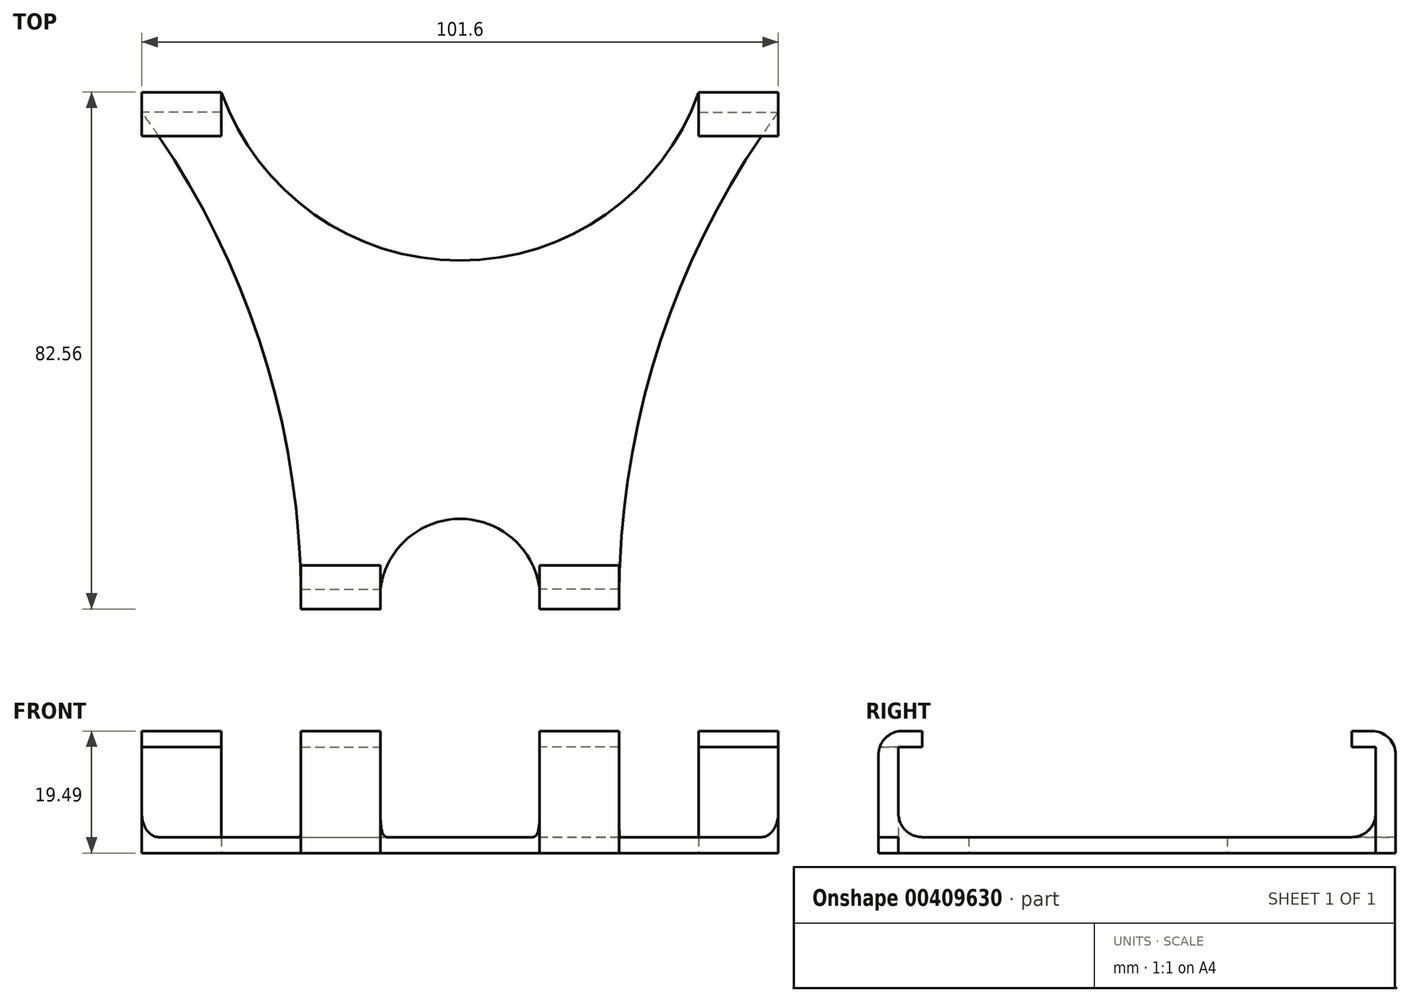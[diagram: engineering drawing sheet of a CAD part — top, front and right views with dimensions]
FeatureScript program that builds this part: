
annotation { "Feature Type Name" : "Feature", "Feature Type Description" : "" }
export const myFeature = defineFeature(function(context is Context, id is Id, definition is map)
    precondition{}
    {
        {
            var Q0;
            Q0=qCreatedBy(makeId("Top.planeOp"),FACE);
            var sketch = newSketch(context, id + "F0", { "sketchPlane" : qUnion([Q0])});
            skPoint(sketch, "E0.middle", {"position": v(0, 0) * mm});
            skLineSegment(sketch, "E1.bottom", {"start": v(-38.1, 38.1) * mm, "end": v(-50.8, 38.1) * mm});
            skLineSegment(sketch, "E1.top", {"start": v(-38.1, 41.27) * mm, "end": v(-50.8, 41.27) * mm});
            skLineSegment(sketch, "E1.left", {"start": v(-38.1, 38.1) * mm, "end": v(-38.1, 41.27) * mm});
            skLineSegment(sketch, "E1.right", {"start": v(-50.8, 38.1) * mm, "end": v(-50.8, 41.27) * mm});
            skLineSegment(sketch, "E2.bottom", {"start": v(-25.4, -38.1) * mm, "end": v(-12.7, -38.1) * mm});
            skLineSegment(sketch, "E2.top", {"start": v(-25.4, -41.28) * mm, "end": v(-12.7, -41.28) * mm});
            skLineSegment(sketch, "E2.left", {"start": v(-25.4, -38.1) * mm, "end": v(-25.4, -41.28) * mm});
            skLineSegment(sketch, "E2.right", {"start": v(-12.7, -38.1) * mm, "end": v(-12.7, -41.28) * mm});
            skLineSegment(sketch, "E3.MirrorCS", {"start": v(50.8, 38.1) * mm, "end": v(50.8, 41.27) * mm});
            skLineSegment(sketch, "E4.MirrorCS", {"start": v(38.1, 38.1) * mm, "end": v(38.1, 41.27) * mm});
            skLineSegment(sketch, "E5.MirrorCS", {"start": v(38.1, 41.27) * mm, "end": v(50.8, 41.27) * mm});
            skLineSegment(sketch, "E6.MirrorCS", {"start": v(38.1, 38.1) * mm, "end": v(50.8, 38.1) * mm});
            skLineSegment(sketch, "E7.MirrorCS", {"start": v(12.7, -38.1) * mm, "end": v(12.7, -41.28) * mm});
            skLineSegment(sketch, "E8.MirrorCS", {"start": v(25.4, -38.1) * mm, "end": v(25.4, -41.28) * mm});
            skLineSegment(sketch, "E9.MirrorCS", {"start": v(25.4, -38.1) * mm, "end": v(12.7, -38.1) * mm});
            skLineSegment(sketch, "E10.MirrorCS", {"start": v(25.4, -41.28) * mm, "end": v(12.7, -41.28) * mm});
            skArc(sketch, "E11", {"start": v(-25.4, -41.28) * mm, "mid": v(-31.66, 0.47) * mm, "end": v(-50.8, 38.1) * mm});
            skArc(sketch, "E12", {"start": v(50.8, 38.1) * mm, "mid": v(31.66, 0.47) * mm, "end": v(25.4, -41.27) * mm});
            skArc(sketch, "E13", {"start": v(-38.1, 41.27) * mm, "mid": v(0, 14.38) * mm, "end": v(38.1, 41.27) * mm});
            skArc(sketch, "E14", {"start": v(12.7, -41.28) * mm, "mid": v(0, -26.89) * mm, "end": v(-12.7, -41.27) * mm});
            skSolve(sketch);
        }
        {
            var Q0;
            Q0=makeQuery(id+"F0.imprint","IMPRINT",FACE,{"disambiguationData":[TD([[makeQuery(id+"F0.imprint","IMPRINT",EDGE,{"derivedFrom":sQuery(id+"F0.wireOp",EDGE,"E1.bottom")}),-1.0]])]});
            var Q1;
            Q1=makeQuery(id+"F0.imprint","IMPRINT",FACE,{"disambiguationData":[TD([[makeQuery(id+"F0.imprint","IMPRINT",EDGE,{"derivedFrom":sQuery(id+"F0.wireOp",EDGE,"E2.bottom")}),-1.0]])]});
            var Q2;
            Q2=makeQuery(id+"F0.imprint","IMPRINT",FACE,{"disambiguationData":[TD([[makeQuery(id+"F0.imprint","IMPRINT",EDGE,{"derivedFrom":sQuery(id+"F0.wireOp",EDGE,"E3.MirrorCS")}),1.0]])]});
            var Q3;
            Q3=makeQuery(id+"F0.imprint","IMPRINT",FACE,{"disambiguationData":[TD([[makeQuery(id+"F0.imprint","IMPRINT",EDGE,{"derivedFrom":sQuery(id+"F0.wireOp",EDGE,"E7.MirrorCS")}),1.0]])]});
            var Q4;
            {var subQ0=sQuery(id+"F0.wireOp",EDGE,"E9.MirrorCS");Q4=makeQuery(id+"F0.imprint","IMPRINT",FACE,{"disambiguationData":[TD([[makeQuery(id+"F0.imprint","IMPRINT",EDGE,{"derivedFrom":subQ0}),1.0]])]});}
            extrude(context, id + "F1", {"entities" : qUnion([Q0, Q1, Q2, Q3, Q4]), "depth" : 16.95 * mm});
        }
        {
            var Q0;
            Q0 = qSketchRegion(id + "F0", true);
            extrude(context, id + "F2", {"entities" : qUnion([Q0]), "operationType" : NewBodyOperationType.ADD, "depth" : 2.54 * mm});
        }
        {
            var Q0;
            Q0=makeQuery(id+"F1.opExtrude","CAP_FACE",FACE,{"disambiguationData":[OSD([sQuery(id+"F0.wireOp",EDGE,"E1.bottom"),sQuery(id+"F0.wireOp",EDGE,"E1.top"),sQuery(id+"F0.wireOp",EDGE,"E1.left"),sQuery(id+"F0.wireOp",EDGE,"E1.right")])],"isStart":false});
            var sketch = newSketch(context, id + "F3", { "sketchPlane" : qUnion([Q0])});
            skLineSegment(sketch, "E15.bottom", {"start": v(-50.8, 41.27) * mm, "end": v(-38.1, 41.27) * mm});
            skLineSegment(sketch, "E15.top", {"start": v(-50.8, 34.29) * mm, "end": v(-38.1, 34.29) * mm});
            skLineSegment(sketch, "E15.left", {"start": v(-50.8, 41.27) * mm, "end": v(-50.8, 34.29) * mm});
            skLineSegment(sketch, "E15.right", {"start": v(-38.1, 41.27) * mm, "end": v(-38.1, 34.29) * mm});
            skLineSegment(sketch, "E16.MirrorCS", {"start": v(50.8, 41.27) * mm, "end": v(38.1, 41.27) * mm});
            skLineSegment(sketch, "E17.MirrorCS", {"start": v(50.8, 41.27) * mm, "end": v(50.8, 34.29) * mm});
            skLineSegment(sketch, "E18.MirrorCS", {"start": v(50.8, 34.29) * mm, "end": v(38.1, 34.29) * mm});
            skLineSegment(sketch, "E19.MirrorCS", {"start": v(38.1, 41.27) * mm, "end": v(38.1, 34.29) * mm});
            skSolve(sketch);
        }
        {
            var Q0;
            Q0 = qSketchRegion(id + "F3", true);
            extrude(context, id + "F4", {"entities" : qUnion([Q0]), "operationType" : NewBodyOperationType.ADD, "depth" : 2.54 * mm});
        }
        {
            var Q0;
            Q0=makeQuery(id+"F1.opExtrude","CAP_FACE",FACE,{"disambiguationData":[OSD([sQuery(id+"F0.wireOp",EDGE,"E2.bottom"),sQuery(id+"F0.wireOp",EDGE,"E2.top"),sQuery(id+"F0.wireOp",EDGE,"E2.left"),sQuery(id+"F0.wireOp",EDGE,"E2.right")])],"isStart":false});
            var sketch = newSketch(context, id + "F5", { "sketchPlane" : qUnion([Q0])});
            skLineSegment(sketch, "E20.bottom", {"start": v(-25.4, -41.28) * mm, "end": v(-12.7, -41.28) * mm});
            skLineSegment(sketch, "E20.top", {"start": v(-25.4, -34.3) * mm, "end": v(-12.7, -34.3) * mm});
            skLineSegment(sketch, "E20.left", {"start": v(-25.4, -41.28) * mm, "end": v(-25.4, -34.3) * mm});
            skLineSegment(sketch, "E20.right", {"start": v(-12.7, -41.28) * mm, "end": v(-12.7, -34.3) * mm});
            skLineSegment(sketch, "E21.MirrorCS", {"start": v(12.7, -41.28) * mm, "end": v(12.7, -34.3) * mm});
            skLineSegment(sketch, "E22.MirrorCS", {"start": v(25.4, -41.28) * mm, "end": v(25.4, -34.3) * mm});
            skLineSegment(sketch, "E23.MirrorCS", {"start": v(25.4, -41.28) * mm, "end": v(12.7, -41.28) * mm});
            skLineSegment(sketch, "E24.MirrorCS", {"start": v(25.4, -34.3) * mm, "end": v(12.7, -34.3) * mm});
            skSolve(sketch);
        }
        {
            var Q0;
            Q0 = qSketchRegion(id + "F5", true);
            extrude(context, id + "F6", {"entities" : qUnion([Q0]), "operationType" : NewBodyOperationType.ADD, "depth" : 2.54 * mm});
        }
        {
            var Q0;
            Q0=makeQuery(id+"F2.boolean.opBoolean","INTERSECT",EDGE,{"derivedFrom":[makeQuery(id+"F1.opExtrude","SWEPT_FACE",FACE,{"disambiguationData":[OSD([sQuery(id+"F0.wireOp",EDGE,"E1.bottom")])]}),makeQuery(id+"F2.opExtrude","CAP_FACE",FACE,{"disambiguationData":[OSD([sQuery(id+"F0.wireOp",EDGE,"E1.top"),sQuery(id+"F0.wireOp",EDGE,"E1.right"),sQuery(id+"F0.wireOp",EDGE,"E2.top"),sQuery(id+"F0.wireOp",EDGE,"E3.MirrorCS"),sQuery(id+"F0.wireOp",EDGE,"E5.MirrorCS"),sQuery(id+"F0.wireOp",EDGE,"E10.MirrorCS"),sQuery(id+"F0.wireOp",EDGE,"hXJoZnsT-Lg7h-pbVR-MQxj-FSggZeGGHfwX"),sQuery(id+"F0.wireOp",EDGE,"yavpTBRq-CuO9-Qr0M-t35S-z9Fk4aJHSNEh"),sQuery(id+"F0.wireOp",EDGE,"0S22i0gG-gJf3-JBYY-297k-QcKDuxpLSIet"),sQuery(id+"F0.wireOp",EDGE,"gkpGqHkD-Pt0P-Dbue-5Zzd-4DBEraHI7jx1")])],"isStart":false})]});
            var Q1;
            Q1=makeQuery(id+"F1.opExtrude","CAP_EDGE",EDGE,{"disambiguationData":[OSD([sQuery(id+"F0.wireOp",EDGE,"E1.bottom")])],"isStart":false});
            var Q2;
            Q2=makeQuery(id+"F2.boolean.opBoolean","INTERSECT",EDGE,{"derivedFrom":[makeQuery(id+"F1.opExtrude","SWEPT_FACE",FACE,{"disambiguationData":[OSD([sQuery(id+"F0.wireOp",EDGE,"E6.MirrorCS")])]}),makeQuery(id+"F2.opExtrude","CAP_FACE",FACE,{"disambiguationData":[OSD([sQuery(id+"F0.wireOp",EDGE,"E1.top"),sQuery(id+"F0.wireOp",EDGE,"E1.right"),sQuery(id+"F0.wireOp",EDGE,"E2.top"),sQuery(id+"F0.wireOp",EDGE,"E3.MirrorCS"),sQuery(id+"F0.wireOp",EDGE,"E5.MirrorCS"),sQuery(id+"F0.wireOp",EDGE,"E10.MirrorCS"),sQuery(id+"F0.wireOp",EDGE,"hXJoZnsT-Lg7h-pbVR-MQxj-FSggZeGGHfwX"),sQuery(id+"F0.wireOp",EDGE,"yavpTBRq-CuO9-Qr0M-t35S-z9Fk4aJHSNEh"),sQuery(id+"F0.wireOp",EDGE,"0S22i0gG-gJf3-JBYY-297k-QcKDuxpLSIet"),sQuery(id+"F0.wireOp",EDGE,"gkpGqHkD-Pt0P-Dbue-5Zzd-4DBEraHI7jx1")])],"isStart":false})]});
            var Q3;
            Q3=makeQuery(id+"F1.opExtrude","CAP_EDGE",EDGE,{"disambiguationData":[OSD([sQuery(id+"F0.wireOp",EDGE,"E6.MirrorCS")])],"isStart":false});
            var Q4;
            Q4=makeQuery(id+"F2.boolean.opBoolean","INTERSECT",EDGE,{"derivedFrom":[makeQuery(id+"F1.opExtrude","SWEPT_FACE",FACE,{"disambiguationData":[OSD([sQuery(id+"F0.wireOp",EDGE,"E2.bottom")])]}),makeQuery(id+"F2.opExtrude","CAP_FACE",FACE,{"disambiguationData":[OSD([sQuery(id+"F0.wireOp",EDGE,"E1.top"),sQuery(id+"F0.wireOp",EDGE,"E1.right"),sQuery(id+"F0.wireOp",EDGE,"E2.top"),sQuery(id+"F0.wireOp",EDGE,"E3.MirrorCS"),sQuery(id+"F0.wireOp",EDGE,"E5.MirrorCS"),sQuery(id+"F0.wireOp",EDGE,"E10.MirrorCS"),sQuery(id+"F0.wireOp",EDGE,"hXJoZnsT-Lg7h-pbVR-MQxj-FSggZeGGHfwX"),sQuery(id+"F0.wireOp",EDGE,"yavpTBRq-CuO9-Qr0M-t35S-z9Fk4aJHSNEh"),sQuery(id+"F0.wireOp",EDGE,"0S22i0gG-gJf3-JBYY-297k-QcKDuxpLSIet"),sQuery(id+"F0.wireOp",EDGE,"gkpGqHkD-Pt0P-Dbue-5Zzd-4DBEraHI7jx1")])],"isStart":false})]});
            var Q5;
            Q5=makeQuery(id+"F2.boolean.opBoolean","INTERSECT",EDGE,{"derivedFrom":[makeQuery(id+"F1.opExtrude","SWEPT_FACE",FACE,{"disambiguationData":[OSD([sQuery(id+"F0.wireOp",EDGE,"E9.MirrorCS")])]}),makeQuery(id+"F2.opExtrude","CAP_FACE",FACE,{"disambiguationData":[OSD([sQuery(id+"F0.wireOp",EDGE,"E1.top"),sQuery(id+"F0.wireOp",EDGE,"E1.right"),sQuery(id+"F0.wireOp",EDGE,"E2.top"),sQuery(id+"F0.wireOp",EDGE,"E3.MirrorCS"),sQuery(id+"F0.wireOp",EDGE,"E5.MirrorCS"),sQuery(id+"F0.wireOp",EDGE,"E10.MirrorCS"),sQuery(id+"F0.wireOp",EDGE,"hXJoZnsT-Lg7h-pbVR-MQxj-FSggZeGGHfwX"),sQuery(id+"F0.wireOp",EDGE,"yavpTBRq-CuO9-Qr0M-t35S-z9Fk4aJHSNEh"),sQuery(id+"F0.wireOp",EDGE,"0S22i0gG-gJf3-JBYY-297k-QcKDuxpLSIet"),sQuery(id+"F0.wireOp",EDGE,"gkpGqHkD-Pt0P-Dbue-5Zzd-4DBEraHI7jx1")])],"isStart":false})]});
            var Q6;
            Q6=makeQuery(id+"F1.opExtrude","CAP_EDGE",EDGE,{"disambiguationData":[OSD([sQuery(id+"F0.wireOp",EDGE,"E9.MirrorCS")])],"isStart":false});
            var Q7;
            Q7=makeQuery(id+"F1.opExtrude","CAP_EDGE",EDGE,{"disambiguationData":[OSD([sQuery(id+"F0.wireOp",EDGE,"E2.bottom")])],"isStart":false});
            var Q8;
            Q8=makeQuery(id+"F4.opExtrude","CAP_EDGE",EDGE,{"disambiguationData":[OSD([sQuery(id+"F3.wireOp",EDGE,"E15.bottom")])],"isStart":false});
            var Q9;
            Q9=makeQuery(id+"F4.opExtrude","CAP_EDGE",EDGE,{"disambiguationData":[OSD([sQuery(id+"F3.wireOp",EDGE,"E16.MirrorCS")])],"isStart":false});
            var Q10;
            Q10=makeQuery(id+"F6.opExtrude","CAP_EDGE",EDGE,{"disambiguationData":[OSD([sQuery(id+"F5.wireOp",EDGE,"E23.MirrorCS")])],"isStart":false});
            var Q11;
            Q11=makeQuery(id+"F6.opExtrude","CAP_EDGE",EDGE,{"disambiguationData":[OSD([sQuery(id+"F5.wireOp",EDGE,"E20.bottom")])],"isStart":false});
            fillet(context, id + "F7", {"entities" : qUnion([Q0, Q1, Q2, Q3, Q4, Q5, Q6, Q7, Q8, Q9, Q10, Q11]), "radius" : 3.8 * mm, "tangentPropagation" : true, "allowEdgeOverflow" : false});
        }
    });
